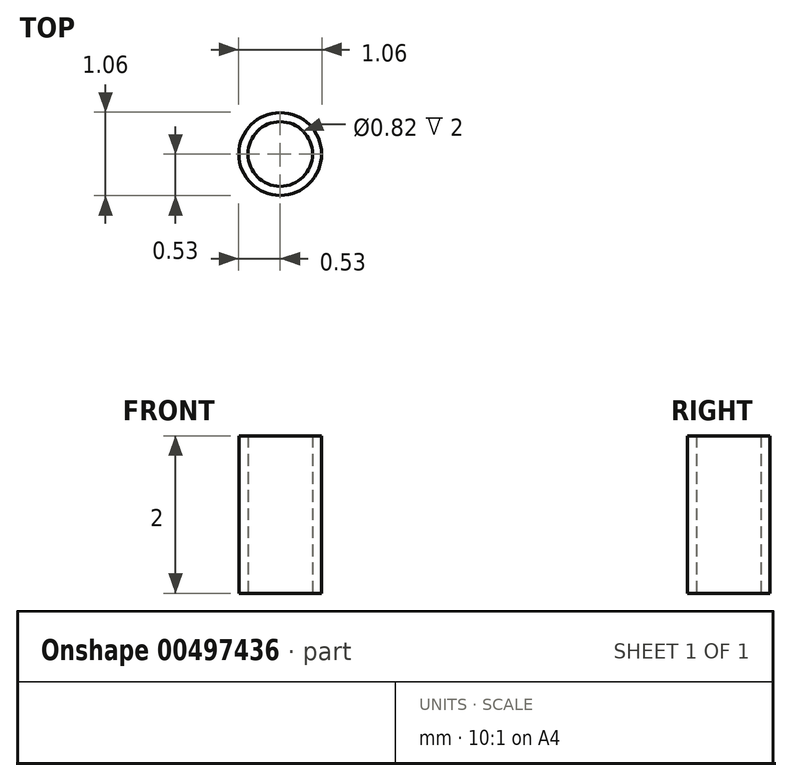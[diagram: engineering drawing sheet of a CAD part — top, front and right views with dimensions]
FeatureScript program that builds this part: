
annotation { "Feature Type Name" : "Feature", "Feature Type Description" : "" }
export const myFeature = defineFeature(function(context is Context, id is Id, definition is map)
    precondition{}
    {
        {
            var Q0;
            Q0=qCreatedBy(makeId("Top.planeOp"),FACE);
            var sketch = newSketch(context, id + "F0", { "sketchPlane" : qUnion([Q0])});
            skCircle(sketch, "E0", {"center": v(0, 0) * mm, "radius": 0.41 * mm});
            skCircle(sketch, "E1", {"center": v(0, 0) * mm, "radius": 0.53 * mm});
            skSolve(sketch);
        }
        {
            var Q0;
            Q0=makeQuery(id+"F0.imprint","IMPRINT",FACE,{"disambiguationData":[TD([[makeQuery(id+"F0.imprint","IMPRINT",EDGE,{"derivedFrom":sQuery(id+"F0.wireOp",EDGE,"E0")}),-1.0]])]});
            extrude(context, id + "F1", {"entities" : qUnion([Q0]), "depth" : 2 * mm});
        }
    });
